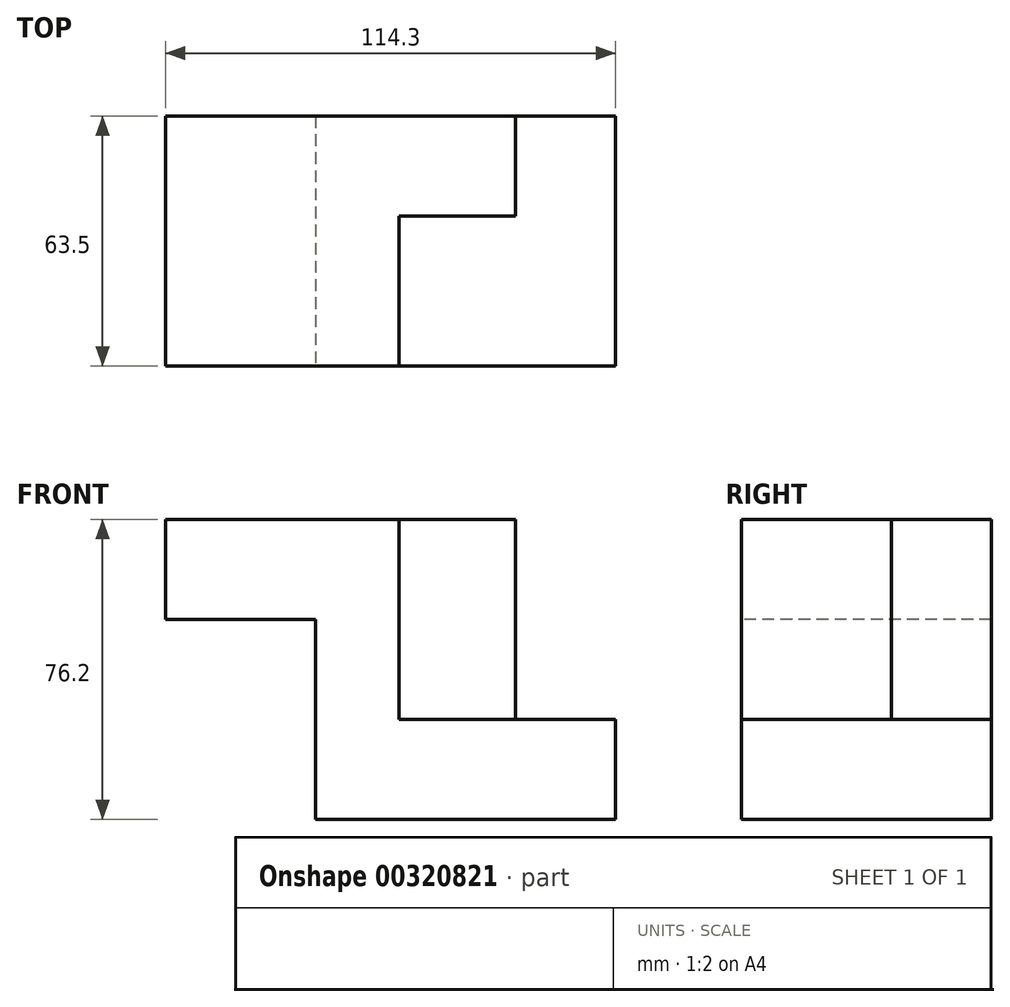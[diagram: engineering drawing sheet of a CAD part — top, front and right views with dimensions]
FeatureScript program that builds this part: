
annotation { "Feature Type Name" : "Feature", "Feature Type Description" : "" }
export const myFeature = defineFeature(function(context is Context, id is Id, definition is map)
    precondition{}
    {
        {
            var Q0;
            Q0=qCreatedBy(makeId("Front.planeOp"),FACE);
            var sketch = newSketch(context, id + "F0", { "sketchPlane" : qUnion([Q0])});
            skLineSegment(sketch, "E0", {"start": v(-59.34, 19.2) * mm, "end": v(-21.24, 19.2) * mm});
            skLineSegment(sketch, "E1", {"start": v(-21.24, 19.2) * mm, "end": v(-21.24, -31.6) * mm});
            skLineSegment(sketch, "E2", {"start": v(-21.24, -31.6) * mm, "end": v(54.96, -31.6) * mm});
            skLineSegment(sketch, "E3", {"start": v(54.96, -31.6) * mm, "end": v(54.96, -6.2) * mm});
            skLineSegment(sketch, "E4", {"start": v(54.96, -6.2) * mm, "end": v(4.16, -6.2) * mm});
            skLineSegment(sketch, "E5", {"start": v(4.16, -6.2) * mm, "end": v(4.16, 44.6) * mm});
            skLineSegment(sketch, "E6", {"start": v(4.16, 44.6) * mm, "end": v(-59.34, 44.6) * mm});
            skLineSegment(sketch, "E7", {"start": v(-59.34, 44.6) * mm, "end": v(-59.34, 19.2) * mm});
            skSolve(sketch);
        }
        {
            var Q0;
            Q0=makeQuery(id+"F0.imprint","IMPRINT",FACE,{"disambiguationData":[TD([[makeQuery(id+"F0.imprint","IMPRINT",EDGE,{"derivedFrom":sQuery(id+"F0.wireOp",EDGE,"E0")}),1.0]])]});
            extrude(context, id + "F1", {"entities" : qUnion([Q0]), "oppositeDirection" : true, "depth" : 63.5 * mm});
        }
        {
            var Q0;
            Q0=makeQuery(id+"F1.opExtrude","SWEPT_FACE",FACE,{"disambiguationData":[OSD([sQuery(id+"F0.wireOp",EDGE,"E5")])]});
            var sketch = newSketch(context, id + "F2", { "sketchPlane" : qUnion([Q0])});
            skLineSegment(sketch, "E8", {"start": v(0, 44.6) * mm, "end": v(63.5, 44.6) * mm});
            skLineSegment(sketch, "E9", {"start": v(63.5, 44.6) * mm, "end": v(63.5, -6.2) * mm});
            skLineSegment(sketch, "E10", {"start": v(63.5, -6.2) * mm, "end": v(0, -6.2) * mm});
            skLineSegment(sketch, "E11", {"start": v(0, -6.2) * mm, "end": v(0, 44.6) * mm});
            skSolve(sketch);
        }
        {
            var Q0;
            Q0=makeQuery(id+"F2.imprint","IMPRINT",FACE,{"disambiguationData":[TD([[makeQuery(id+"F2.imprint","IMPRINT",EDGE,{"derivedFrom":sQuery(id+"F2.wireOp",EDGE,"E8")}),1.0]])]});
            extrude(context, id + "F3", {"entities" : qUnion([Q0]), "operationType" : NewBodyOperationType.ADD, "depth" : 25.4 * mm});
        }
        {
            var Q0;
            Q0=makeQuery(id+"F3.boolean.opBoolean","MERGE",FACE,{"derivedFrom":[makeQuery(id+"F1.opExtrude","SWEPT_FACE",FACE,{"disambiguationData":[OSD([sQuery(id+"F0.wireOp",EDGE,"E6")])]}),makeQuery(id+"F3.opExtrude","SWEPT_FACE",FACE,{"disambiguationData":[OSD([sQuery(id+"F2.wireOp",EDGE,"E8")])]})]});
            var sketch = newSketch(context, id + "F4", { "sketchPlane" : qUnion([Q0])});
            skLineSegment(sketch, "E12", {"start": v(0, 0) * mm, "end": v(0, 38.1) * mm});
            skLineSegment(sketch, "E13", {"start": v(0, 38.1) * mm, "end": v(29.56, 38.1) * mm});
            skLineSegment(sketch, "E14", {"start": v(29.56, 38.1) * mm, "end": v(29.56, 0) * mm});
            skLineSegment(sketch, "E15", {"start": v(29.56, 0) * mm, "end": v(0, 0) * mm});
            skSolve(sketch);
        }
        {
            var Q0;
            Q0=makeQuery(id+"F4.imprint","IMPRINT",FACE,{"disambiguationData":[TD([[makeQuery(id+"F4.imprint","IMPRINT",EDGE,{"derivedFrom":sQuery(id+"F4.wireOp",EDGE,"E12")}),-1.0]])]});
            extrude(context, id + "F5", {"entities" : qUnion([Q0]), "operationType" : NewBodyOperationType.REMOVE, "oppositeDirection" : true, "depth" : 50.8 * mm});
        }
    });
